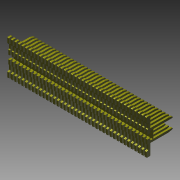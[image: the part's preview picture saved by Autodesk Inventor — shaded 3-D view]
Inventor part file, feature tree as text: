
AUTODESK INVENTOR PART (.ipt)
format: ipt  version: 2016 (Build 200138000, 138)  size: 1,467,904 bytes
history: native  units: mm
features: other x7, extrude x2, sketch x2
ambient origin geometry x8: Origin, YZ Plane, XZ Plane, XY Plane, X Axis, Y Axis, Z Axis, Center Point
bodies: Solid1 (feature_tree)
feature tree (11):
  extrude  "Extrusion1"  Depth=4.2mm TaperAngle=0.0deg
  extrude  "Extrusion2"  [1 undecoded]
  other  "pin_XY"
  other  "pin_YZ"
  other  "pin_ZX"
  other  "pin_X"
  other  "pin_Y"
  other  "pin_Z"
  other  "pin_Center"
  sketch  "Sketch_1"  dims[d0=4.2mm d1=0.0mm d2=80.0mm d3=0.0mm]
  sketch  "Sketch_2"
note: 1 required parameter value undecoded (feature->parameter linkage not recoverable at this tier; creation-order binding heuristic only, values carry confidence <= 0.55)
